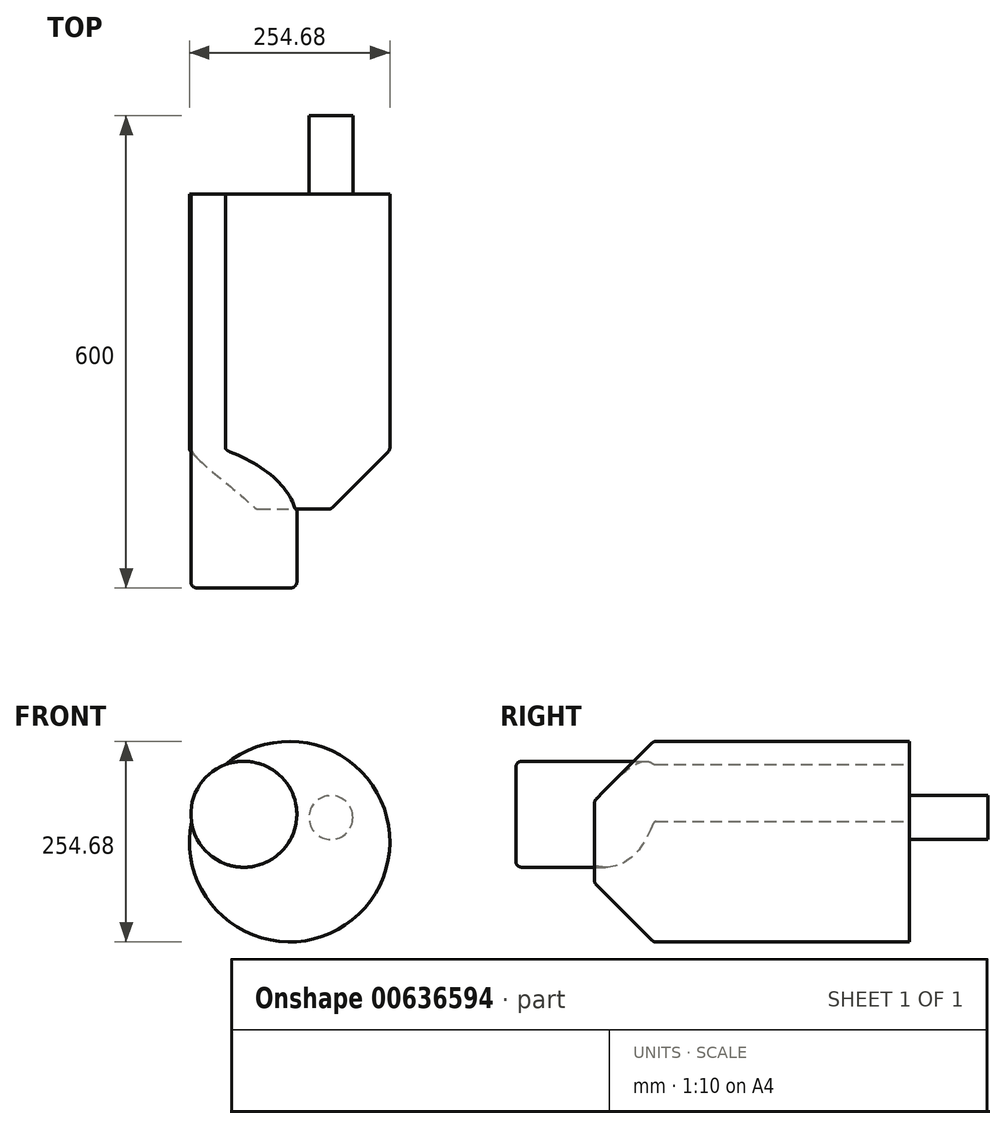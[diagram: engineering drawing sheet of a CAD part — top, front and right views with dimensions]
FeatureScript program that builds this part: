
annotation { "Feature Type Name" : "Feature", "Feature Type Description" : "" }
export const myFeature = defineFeature(function(context is Context, id is Id, definition is map)
    precondition{}
    {
        {
            var Q0;
            Q0=qCreatedBy(makeId("Front.planeOp"),FACE);
            var sketch = newSketch(context, id + "F0", { "sketchPlane" : qUnion([Q0])});
            skCircle(sketch, "E0", {"center": v(0, 0) * mm, "radius": 127.34 * mm});
            skCircle(sketch, "E1", {"center": v(52.57, 30.7) * mm, "radius": 27.87 * mm});
            skCircle(sketch, "E2", {"center": v(-58.06, 34.78) * mm, "radius": 67.31 * mm});
            skSolve(sketch);
        }
        {
            var Q0;
            {var subQ0=sQuery(id+"F0.wireOp",EDGE,"E2");var subQ1=sQuery(id+"F0.wireOp",EDGE,"E0");var subQ2=makeQuery(id+"F0.imprint","INTERSECT",VERTEX,{"disambiguationData":[OD(0.0)],"derivedFrom":[subQ1,subQ0]});Q0=makeQuery(id+"F0.imprint","IMPRINT",FACE,{"disambiguationData":[TD([[makeQuery(id+"F0.imprint","IMPRINT",EDGE,{"disambiguationData":[TD([[subQ2,1.0]])],"derivedFrom":subQ1}),1.0]])]});}
            var Q1;
            {var subQ0=sQuery(id+"F0.wireOp",EDGE,"E2");var subQ1=sQuery(id+"F0.wireOp",EDGE,"E0");var subQ2=makeQuery(id+"F0.imprint","INTERSECT",VERTEX,{"disambiguationData":[OD(0.0)],"derivedFrom":[subQ1,subQ0]});Q1=makeQuery(id+"F0.imprint","IMPRINT",FACE,{"disambiguationData":[TD([[makeQuery(id+"F0.imprint","IMPRINT",EDGE,{"disambiguationData":[TD([[subQ2,1.0]])],"derivedFrom":subQ1}),-1.0]])]});}
            extrude(context, id + "F1", {"entities" : qUnion([Q0, Q1]), "depth" : 500 * mm, "offsetDistance" : 25.4 * mm});
        }
        {
            var Q0;
            Q0=makeQuery(id+"F0.imprint","IMPRINT",FACE,{"disambiguationData":[TD([[makeQuery(id+"F0.imprint","IMPRINT",EDGE,{"derivedFrom":sQuery(id+"F0.wireOp",EDGE,"E1")}),-1.0]])]});
            var Q1;
            Q1=makeQuery(id+"F0.imprint","IMPRINT",FACE,{"disambiguationData":[TD([[makeQuery(id+"F0.imprint","IMPRINT",EDGE,{"derivedFrom":sQuery(id+"F0.wireOp",EDGE,"E1")}),1.0]])]});
            extrude(context, id + "F2", {"entities" : qUnion([Q0, Q1]), "operationType" : NewBodyOperationType.ADD, "depth" : 400 * mm, "offsetDistance" : 25.4 * mm});
        }
        {
            var Q0;
            Q0=makeQuery(id+"F0.imprint","IMPRINT",FACE,{"disambiguationData":[TD([[makeQuery(id+"F0.imprint","IMPRINT",EDGE,{"derivedFrom":sQuery(id+"F0.wireOp",EDGE,"E1")}),1.0]])]});
            extrude(context, id + "F3", {"entities" : qUnion([Q0]), "operationType" : NewBodyOperationType.ADD, "oppositeDirection" : true, "depth" : 100 * mm, "offsetDistance" : 25.4 * mm});
        }
        {
            var Q0;
            Q0=makeQuery(id+"F2.opExtrude","CAP_EDGE",EDGE,{"disambiguationData":[OSD([sQuery(id+"F0.wireOp",EDGE,"E0")])],"isStart":false});
            chamfer(context, id + "F4", {"entities" : qUnion([Q0]), "width" : 75 * mm, "tangentPropagation" : true});
        }
        {
            var Q0;
            Q0=makeQuery(id+"F1.opExtrude","CAP_EDGE",EDGE,{"disambiguationData":[OSD([sQuery(id+"F0.wireOp",EDGE,"E2")])],"isStart":false});
            fillet(context, id + "F5", {"entities" : qUnion([Q0]), "radius" : 7.62 * mm, "tangentPropagation" : true, "allowEdgeOverflow" : false});
        }
        {
            var Q0;
            {var subQ0=sQuery(id+"F0.wireOp",EDGE,"E0");Q0=makeQuery(id+"F4.opChamfer","BLEND_EDGE",EDGE,{"blendedFrom":[makeQuery(id+"F2.opExtrude","CAP_EDGE",EDGE,{"disambiguationData":[OSD([subQ0])],"isStart":false}),makeQuery(id+"F2.opExtrude","CAP_FACE",FACE,{"disambiguationData":[OSD([subQ0,sQuery(id+"F0.wireOp",EDGE,"E2")])],"isStart":false})],"blendedInto":[makeQuery(id+"F2.opExtrude","CAP_FACE",FACE,{"disambiguationData":[OSD([subQ0,sQuery(id+"F0.wireOp",EDGE,"E2")])],"isStart":false})]});}
            fillet(context, id + "F6", {"entities" : qUnion([Q0]), "radius" : 7.62 * mm, "tangentPropagation" : true, "allowEdgeOverflow" : false});
        }
        {
            var Q0;
            {var subQ0=sQuery(id+"F0.wireOp",EDGE,"E0");Q0=makeQuery(id+"F4.opChamfer","BLEND_EDGE",EDGE,{"blendedFrom":[makeQuery(id+"F2.opExtrude","CAP_EDGE",EDGE,{"disambiguationData":[OSD([subQ0])],"isStart":false}),makeQuery(id+"F2.opExtrude","SWEPT_FACE",FACE,{"disambiguationData":[OSD([subQ0])]})],"blendedInto":[makeQuery(id+"F2.opExtrude","SWEPT_FACE",FACE,{"disambiguationData":[OSD([subQ0])]})]});}
            fillet(context, id + "F7", {"entities" : qUnion([Q0]), "radius" : 7.62 * mm, "tangentPropagation" : true, "allowEdgeOverflow" : false});
        }
    });
